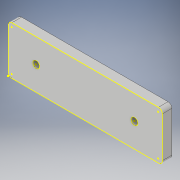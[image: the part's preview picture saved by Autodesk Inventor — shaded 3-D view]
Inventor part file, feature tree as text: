
AUTODESK INVENTOR PART (.ipt)
format: ipt  version: 2019 (Build 230136000, 136)  size: 116,736 bytes
history: native  units: mm
features: sketch x3, extrude x1, hole x1, fillet x1, projected_geometry x1
ambient origin geometry x8: Origin, YZ Plane, XZ Plane, XY Plane, X Axis, Y Axis, Z Axis, Center Point
bodies: Solid1 (feature_tree)
feature tree (7):
  sketch  "Sketch1"  dims[d0=80.0mm d1=25.0mm]
  extrude  "Extrusion1"  Depth=25.0mm
  hole  "Hole1"  [1 undecoded]
  fillet  "Fillet1"  Radius=51.0mm
  sketch  "Sketch3"  dims[d5=80.0mm d6=25.0mm d7=12.5mm d8=14.5mm d9=51.0mm d10=5.0mm d11=0.0mm d12=3.5mm d13=6.0mm d14=4.0mm d15=2.0mm d16=90.0deg d17=8.0mm d18=20.594885mm d19=2.0mm]
  sketch  "Sketch2"  dims[d2=12.5mm d3=14.5mm d4=51.0mm]
  projected_geometry  "Projected Loop1"
note: 1 required parameter value undecoded (feature->parameter linkage not recoverable at this tier; creation-order binding heuristic only, values carry confidence <= 0.55)
